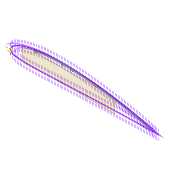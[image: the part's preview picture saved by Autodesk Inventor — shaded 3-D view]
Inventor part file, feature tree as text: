
AUTODESK INVENTOR PART (.ipt)
format: ipt  version: 2022 (Build 260153000, 153)  size: 479,232 bytes
history: native  units: mm
features: projected_geometry x8, extrude x7, sketch x7, shell x1, plane x1, chamfer x1
ambient origin geometry x8: Origin, YZ Plane, XZ Plane, XY Plane, X Axis, Y Axis, Z Axis, Center Point
bodies: Solid1 (feature_tree)
feature tree (25):
  extrude  "Extrusion1"  Depth=4.0mm
  shell  "Shell1"  Thickness=2.0mm
  extrude  "Extrusion8"  Depth=5.9mm
  extrude  "Extrusion3"  Depth=10.0mm TaperAngle=0.0deg
  extrude  "Extrusion4"  Depth=5.0mm
  extrude  "Extrusion5"  Depth=2.5mm
  plane  "Work Plane2"
  extrude  "Extrusion9"  Depth=5.0mm
  chamfer  "Chamfer1"  Distance=77.0mm
  extrude  "Extrusion12"  Depth=5.0mm
  sketch  "Sketch31"  dims[d37=5.0mm d38=1.6mm]
  sketch  "Sketch32"  dims[d40=2.5mm d62=77.0mm d63=5.0mm d64=2.0mm d65=0.0mm d66=2.5mm d67=12.0mm d68=80.0mm d69=20.0mm d70=0.5mm d71=10.0mm d72=0.0mm d75=3.0mm d76=3.0mm d77=2.0mm d78=45.0deg d80=0.0mm d81=1.0mm d82=1.0mm d83=1.0mm d84=1.0mm d85=1.0mm d88=10.0mm d89=0.0mm]
  sketch  "Sketch3"  dims[d0=2.0mm d1=0.0mm d2=4.0mm d7=2.0mm]
  sketch  "Sketch8"  dims[d8=2.0mm d9=5.9mm]
  sketch  "Sketch9"  dims[d13=10.0mm d14=0.0mm d16=10.0mm d17=0.0mm]
  projected_geometry  "Projected Loop4"
  projected_geometry  "Projected Loop10"
  sketch  "Sketch24"  dims[d22=2.0mm d23=0.0mm d32=5.0mm]
  projected_geometry  "Projected Loop11"
  projected_geometry  "Projected Loop12"
  projected_geometry  "Projected Loop13"
  sketch  "Sketch28"  dims[d34=1.6mm d35=2.5mm]
  projected_geometry  "Project Cut Edges1"
  projected_geometry  "Project Cut Edges4"
  projected_geometry  "Project Cut Edges5"
